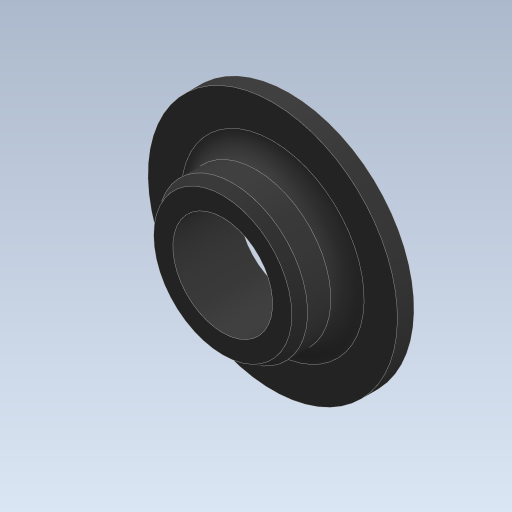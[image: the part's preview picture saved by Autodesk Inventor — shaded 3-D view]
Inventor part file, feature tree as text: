
AUTODESK INVENTOR PART (.ipt)
format: ipt  version: 2024 (Build 280153000, 153)  size: 138,752 bytes
history: native  units: mm
features: other x1, revolve x1, fillet x1, chamfer x1, sketch x1
ambient origin geometry x8: Origin, YZ Plane, XZ Plane, XY Plane, X Axis, Y Axis, Z Axis, Center Point
bodies: Body1 (feature_tree)
feature tree (5):
  other  "ソリッド1"
  revolve  "回転1"
  fillet  "フィレット1"  Radius=3.0mm
  chamfer  "面取り1"  Distance=4.5mm
  sketch  "スケッチ1"
